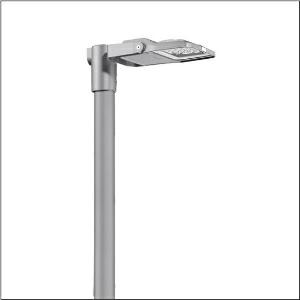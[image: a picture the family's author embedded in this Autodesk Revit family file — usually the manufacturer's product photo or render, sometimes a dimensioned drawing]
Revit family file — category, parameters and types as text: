
# Revit family: floodlight_fl_21_iq_micro___pl61_5xa7761a2c3a_df0f
name_source: partatom
category: Lighting Fixtures
units: mm (PartAtom-declared; Revit-internal decimal feet)

## family parameters
Cut with Voids When Loaded = No
Host = Face
Light Source = No
Part Type = Normal
Room Calculation Point = No
Round Connector Dimension = Use Diameter
Shared = No

## types (1)
- --- (1 x LED, 2910 lm, 23.1 W, 3000K)
    Apparent Load = 23 VA
    CIE Flux Codes = 33 65 98 100 100
    Color Rendering = 70
    Color Temperature = 3000K
    Default Elevation = 1800 mm
    Description = Floodlight FL 21 iQ micro, floodlight, primary light control with lens, of PMMA, primary optical cover: protective disc, of toughened safety glass, transparent, light distribution: PL61, light emission: direct distribution, installation type: surface-mounted, lamps: LED, High Power LED, rated values: 2.910lm | 23,1W | 126lm/W (begin service life); end service life: 2.910lm | 23,8W; at 50% lumin. flux: 1.455lm | 11W | 132,3lm/W, colour temperature: 3000K, colour rendering: CRI > 70, light colour: 730, light setting 1 begin service life: 100% | 2.910lm | 23,1W | 126lm/W | 3.000K, light setting 1 end service life: 23,8W, further light settings possible, control: optimised constant luminous flux control (CLO 2.0), Desk-Remote (wireless, voltage-free reading and setting of iQ features in the workshop via application-optimized NFC function/RFID function), Light-Fading, Smart-Wire, Night-Set, Lumen-Switch, Temp-Guard, Auto-Match, pre-setting: linear dimming characteristic, with terminal, 6-pole, mains connection: 220..240V, AC, 50/60Hz, luminaire housing, of diecast aluminium, powder-coated, SITECO metallic grey (DB 702S), corrosivity category C5 mid according to DIN EN ISO 12944suitable for swimming poolschlorine-resistant, sealing non-destructively replaceable, please order mast flange separately, mast bracket, of steel, galvanised, powder-coated, SITECO metallic grey (DB 702S), protection rating (complete): IP66, insulation class (complete): insulation class II (safety insulation), certification: CE, ENEC, VDE, protection symbol: D, impact resistance: IK07, permissible operating ambient temperature: -40..+40°C, permissible operating ambient temperature for outdoor applications: -40..+50°C, standard: DIN EN 12944, LABS conformity tested according to VDMA 24364:2018-05, packaging unit: 1 piece

Light Distribution: PL61
    Height = 65 mm
    Lamp = 1 x LED
    Lamp Light Flux = 2910 lm
    Lamp Power = 23.1 W
    Lamp count = 1
    Length = 312 mm
    Luminous efficacy = 126 lm/W
    Manufacturer = Siteco
    ModVariant = No
    Model = 5XA7761A2C3A
    Mounting Place = Pole
    Mounting Type = Pole top
    Number of Poles = 1
    OnlyDefault = Yes
    Power Factor = 1
    Product Name = Floodlight FL 21 iQ micro | PL61
    Product group = floodlight | pylon top
    ProductGroupID = 6101
    Protection Class = Protection class II
    Protection Degree = IP 66
    RLX_Detail_Level = 1
    RLX_Emergency_Light_Flux = 0 lm
    RLX_Emergency_Type = 0
    RLX_Emergency_Type_DB = No
    RlxData = <blob elided: 102149 chars, md5=af0b6f04>
    Socket = socket
    Standby Power = 0 W
    System Light Flux = 2910 lm
    System Power = 23 W
    Type Comments = factory setting: luminous flux: 100 % | dim-lin: 254 | 455 mA
    Type Image = l_1007121.jpg
    URL = http://relux.com
    VarID = @adj_193641
    Voltage = 0 V
    Weight = 0.00 kg
    Width = 230 mm

## geometry (parser evidence)
native form markers: Blend x4, Sweep x12
no freeform markers — native parametric forms only
